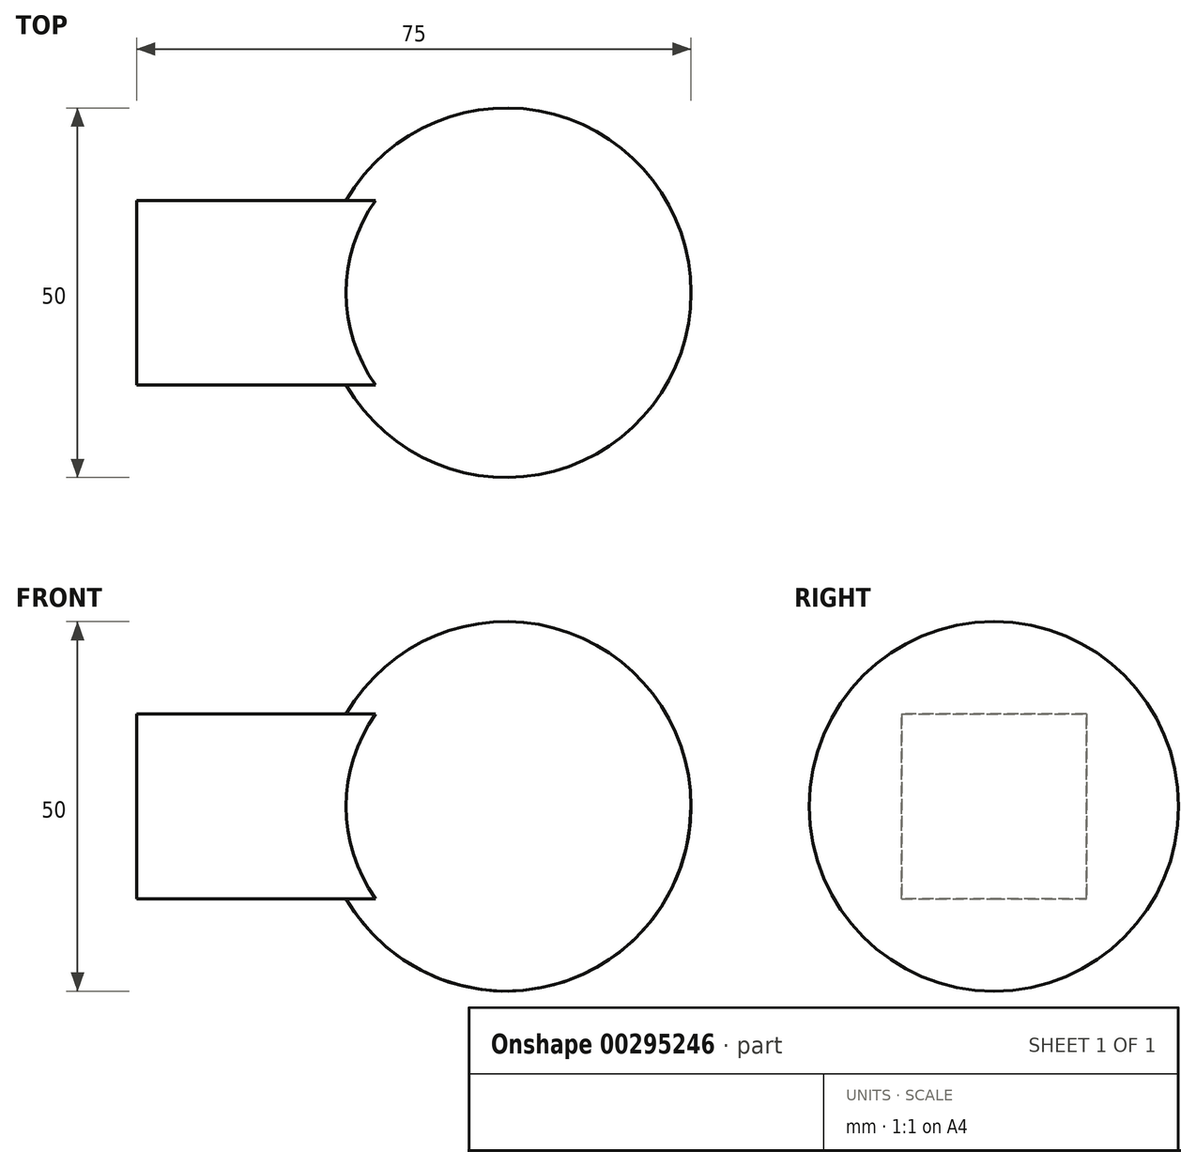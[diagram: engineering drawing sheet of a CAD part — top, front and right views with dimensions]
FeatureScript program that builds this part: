
annotation { "Feature Type Name" : "Feature", "Feature Type Description" : "" }
export const myFeature = defineFeature(function(context is Context, id is Id, definition is map)
    precondition{}
    {
        {
            var Q0;
            Q0=qCreatedBy(makeId("Front.planeOp"),FACE);
            var sketch = newSketch(context, id + "F0", { "sketchPlane" : qUnion([Q0])});
            skLineSegment(sketch, "E0", {"start": v(0, 0) * mm, "end": v(50, 0) * mm});
            skArc(sketch, "E1", {"start": v(75, 0) * mm, "mid": v(56.47, 24.15) * mm, "end": v(28.35, 12.5) * mm});
            skLineSegment(sketch, "E2.left", {"start": v(0, 0) * mm, "end": v(0, 0) * mm});
            skLineSegment(sketch, "E2.right", {"start": v(50, 0) * mm, "end": v(50, 0) * mm});
            skLineSegment(sketch, "E3.bottom", {"start": v(0, 0) * mm, "end": v(25, 0) * mm});
            skLineSegment(sketch, "E3.top", {"start": v(0, 12.5) * mm, "end": v(28.35, 12.5) * mm});
            skLineSegment(sketch, "E3.left", {"start": v(0, 0) * mm, "end": v(0, 12.5) * mm});
            skPoint(sketch, "E3.right.end.orphan", {"position": v(50, 12.5) * mm});
            skLineSegment(sketch, "E4", {"start": v(50, 0) * mm, "end": v(75, 0) * mm});
            skSolve(sketch);
        }
        {
            var Q0;
            Q0 = qSketchRegion(id + "F0", true);
            var Q1;
            Q1=sQuery(id+"F0.wireOp",EDGE,"E3.bottom");
            revolve(context, id + "F1", {"entities" : qUnion([Q0]), "axis" : qUnion([Q1]), "revolveType" : RevolveType.FULL});
        }
        {
            var Q0;
            Q0=makeQuery(id+"F1.opRevolve","SWEPT_FACE",FACE,{"disambiguationData":[OSD([sQuery(id+"F0.wireOp",EDGE,"E3.left")])]});
            var sketch = newSketch(context, id + "F2", { "sketchPlane" : qUnion([Q0])});
            skLineSegment(sketch, "E5.bottom", {"start": v(-12.5, 12.5) * mm, "end": v(12.5, 12.5) * mm});
            skLineSegment(sketch, "E5.top", {"start": v(-12.5, -12.5) * mm, "end": v(12.5, -12.5) * mm});
            skLineSegment(sketch, "E5.left", {"start": v(-12.5, 12.5) * mm, "end": v(-12.5, -12.5) * mm});
            skLineSegment(sketch, "E5.right", {"start": v(12.5, 12.5) * mm, "end": v(12.5, -12.5) * mm});
            skSolve(sketch);
        }
        {
            var Q0;
            Q0 = qSketchRegion(id + "F2", true);
            var Q1;
            Q1=makeQuery(id+"F1.opRevolve","SWEPT_FACE",FACE,{"disambiguationData":[OSD([sQuery(id+"F0.wireOp",EDGE,"E1")])]});
            extrude(context, id + "F3", {"entities" : qUnion([Q0]), "operationType" : NewBodyOperationType.ADD, "endBound" : BoundingType.UP_TO_SURFACE, "oppositeDirection" : true, "endBoundEntityFace" : qUnion([Q1]), "depth" : 25 * mm});
        }
    });
